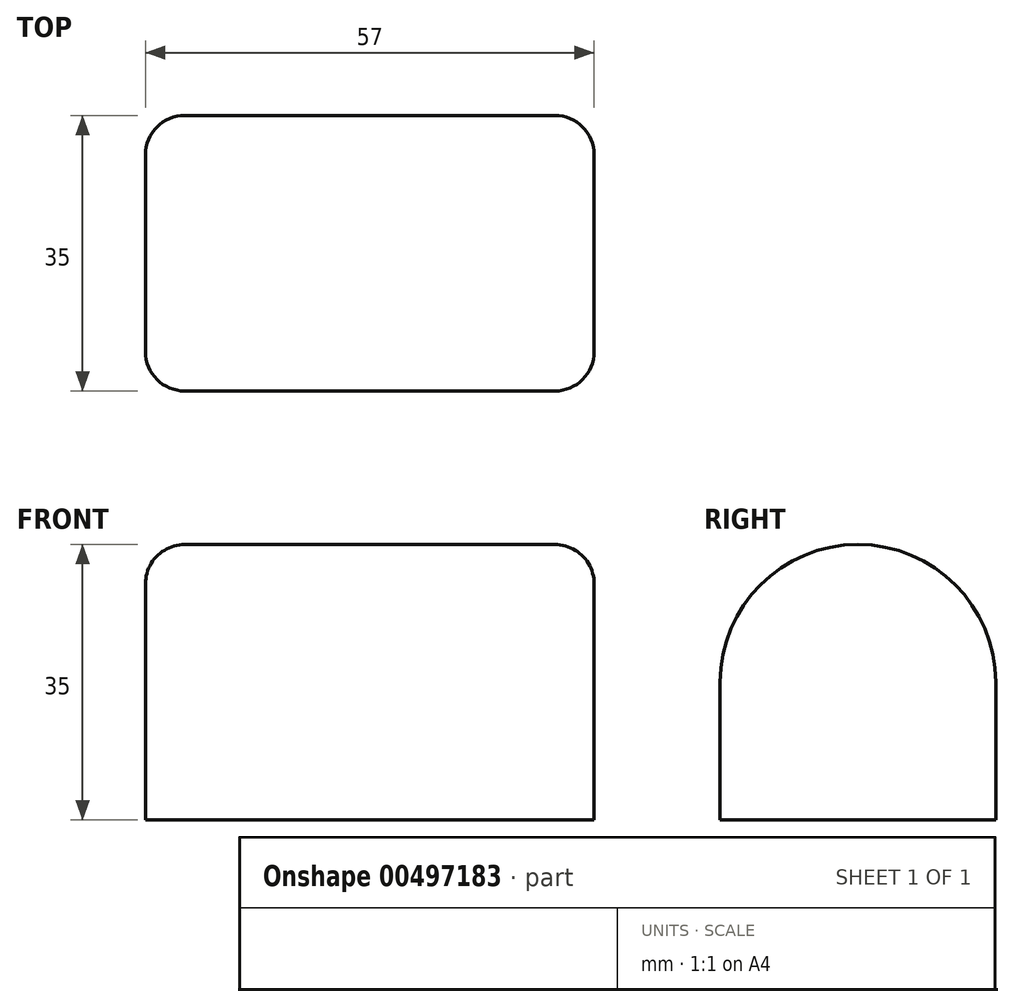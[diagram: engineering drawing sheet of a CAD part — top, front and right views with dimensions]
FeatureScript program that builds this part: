
annotation { "Feature Type Name" : "Feature", "Feature Type Description" : "" }
export const myFeature = defineFeature(function(context is Context, id is Id, definition is map)
    precondition{}
    {
        {
            var Q0;
            Q0=qCreatedBy(makeId("Top.planeOp"),FACE);
            var sketch = newSketch(context, id + "F0", { "sketchPlane" : qUnion([Q0])});
            skLineSegment(sketch, "E0.bottom", {"start": v(-28.5, 17.5) * mm, "end": v(28.5, 17.5) * mm});
            skLineSegment(sketch, "E0.top", {"start": v(-28.5, -17.5) * mm, "end": v(28.5, -17.5) * mm});
            skLineSegment(sketch, "E0.left", {"start": v(-28.5, 17.5) * mm, "end": v(-28.5, -17.5) * mm});
            skLineSegment(sketch, "E0.right", {"start": v(28.5, 17.5) * mm, "end": v(28.5, -17.5) * mm});
            skPoint(sketch, "E0.middle", {"position": v(0, 0) * mm});
            skSolve(sketch);
        }
        {
            var Q0;
            Q0=makeQuery(id+"F0.imprint","IMPRINT",FACE,{"disambiguationData":[TD([[makeQuery(id+"F0.imprint","IMPRINT",EDGE,{"derivedFrom":sQuery(id+"F0.wireOp",EDGE,"E0.bottom")}),-1.0]])]});
            extrude(context, id + "F1", {"entities" : qUnion([Q0]), "depth" : 35 * mm, "offsetDistance" : 25 * mm});
        }
        {
            var Q0;
            Q0=makeQuery(id+"F1.opExtrude","CAP_EDGE",EDGE,{"disambiguationData":[OSD([sQuery(id+"F0.wireOp",EDGE,"E0.top")])],"isStart":false});
            var Q1;
            Q1=makeQuery(id+"F1.opExtrude","CAP_EDGE",EDGE,{"disambiguationData":[OSD([sQuery(id+"F0.wireOp",EDGE,"E0.bottom")])],"isStart":false});
            fillet(context, id + "F2", {"entities" : qUnion([Q0, Q1]), "radius" : 17.5 * mm, "tangentPropagation" : true, "allowEdgeOverflow" : false});
        }
        {
            var Q0;
            Q0=makeQuery(id+"F1.opExtrude","SWEPT_EDGE",EDGE,{"disambiguationData":[OSD([sQuery(id+"F0.wireOp",EDGE,"E0.bottom"),sQuery(id+"F0.wireOp",EDGE,"E0.right")])]});
            var Q1;
            Q1=makeQuery(id+"F2.opFillet","BLEND_EDGE",EDGE,{"blendedFrom":[makeQuery(id+"F1.opExtrude","CAP_EDGE",EDGE,{"disambiguationData":[OSD([sQuery(id+"F0.wireOp",EDGE,"E0.bottom")])],"isStart":false}),makeQuery(id+"F1.opExtrude","SWEPT_FACE",FACE,{"disambiguationData":[OSD([sQuery(id+"F0.wireOp",EDGE,"E0.right")])]})],"blendedInto":[makeQuery(id+"F1.opExtrude","SWEPT_FACE",FACE,{"disambiguationData":[OSD([sQuery(id+"F0.wireOp",EDGE,"E0.right")])]})]});
            var Q2;
            Q2=makeQuery(id+"F1.opExtrude","SWEPT_EDGE",EDGE,{"disambiguationData":[OSD([sQuery(id+"F0.wireOp",EDGE,"E0.top"),sQuery(id+"F0.wireOp",EDGE,"E0.right")])]});
            var Q3;
            Q3=makeQuery(id+"F2.opFillet","BLEND_EDGE",EDGE,{"blendedFrom":[makeQuery(id+"F1.opExtrude","CAP_EDGE",EDGE,{"disambiguationData":[OSD([sQuery(id+"F0.wireOp",EDGE,"E0.bottom")])],"isStart":false}),makeQuery(id+"F1.opExtrude","SWEPT_FACE",FACE,{"disambiguationData":[OSD([sQuery(id+"F0.wireOp",EDGE,"E0.left")])]})],"blendedInto":[makeQuery(id+"F1.opExtrude","SWEPT_FACE",FACE,{"disambiguationData":[OSD([sQuery(id+"F0.wireOp",EDGE,"E0.left")])]})]});
            var Q4;
            Q4=makeQuery(id+"F1.opExtrude","SWEPT_EDGE",EDGE,{"disambiguationData":[OSD([sQuery(id+"F0.wireOp",EDGE,"E0.top"),sQuery(id+"F0.wireOp",EDGE,"E0.left")])]});
            var Q5;
            Q5=makeQuery(id+"F1.opExtrude","SWEPT_EDGE",EDGE,{"disambiguationData":[OSD([sQuery(id+"F0.wireOp",EDGE,"E0.bottom"),sQuery(id+"F0.wireOp",EDGE,"E0.left")])]});
            fillet(context, id + "F3", {"entities" : qUnion([Q0, Q1, Q2, Q3, Q4, Q5]), "radius" : 5 * mm, "tangentPropagation" : true, "allowEdgeOverflow" : false});
        }
    });
